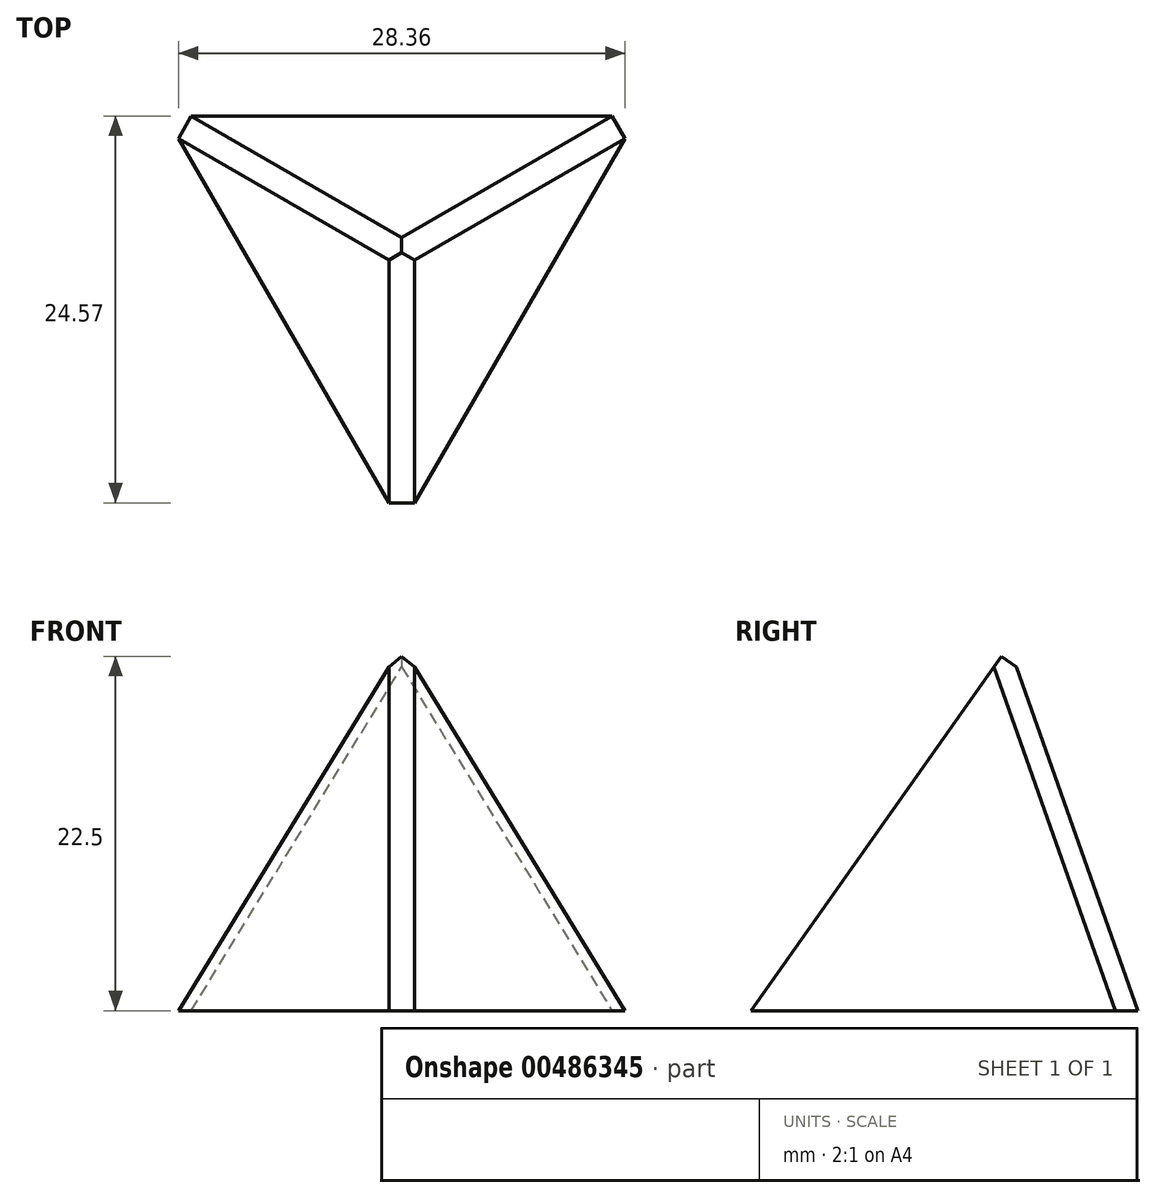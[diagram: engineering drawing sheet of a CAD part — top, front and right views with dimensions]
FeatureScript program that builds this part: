
annotation { "Feature Type Name" : "Feature", "Feature Type Description" : "" }
export const myFeature = defineFeature(function(context is Context, id is Id, definition is map)
    precondition{}
    {
        {
            var Q0;
            Q0=qCreatedBy(makeId("Top.planeOp"),FACE);
            var sketch = newSketch(context, id + "F0", { "sketchPlane" : qUnion([Q0])});
            skCircle(sketch, "E0.cCircle", {"center": v(0, 0) * mm, "radius": 8.66 * mm, "construction": true});
            skLineSegment(sketch, "E0.0", {"start": v(-15, 8.66) * mm, "end": v(15, 8.66) * mm});
            skLineSegment(sketch, "E0.1", {"start": v(15, 8.66) * mm, "end": v(0, -17.32) * mm});
            skLineSegment(sketch, "E0.2", {"start": v(0, -17.32) * mm, "end": v(-15, 8.66) * mm});
            skPoint(sketch, "E0.0.midPoint", {"position": v(0, 8.66) * mm});
            skSolve(sketch);
        }
        {
            var Q0;
            Q0 = qSketchRegion(id + "F0", true);
            extrude(context, id + "F1", {"entities" : qUnion([Q0]), "depth" : 24.5 * mm, "hasDraft" : true, "draftAngle" : 19.47 * degree, "draftPullDirection" : true});
        }
        {
            var Q0;
            Q0=makeQuery(id+"F1.opExtrude","SWEPT_EDGE",EDGE,{"disambiguationData":[OSD([sQuery(id+"F0.wireOp",EDGE,"E0.1"),sQuery(id+"F0.wireOp",EDGE,"E0.2")])]});
            var Q1;
            Q1=makeQuery(id+"F1.opExtrude","SWEPT_EDGE",EDGE,{"disambiguationData":[OSD([sQuery(id+"F0.wireOp",EDGE,"E0.0"),sQuery(id+"F0.wireOp",EDGE,"E0.1")])]});
            var Q2;
            Q2=makeQuery(id+"F1.opExtrude","SWEPT_EDGE",EDGE,{"disambiguationData":[OSD([sQuery(id+"F0.wireOp",EDGE,"E0.0"),sQuery(id+"F0.wireOp",EDGE,"E0.2")])]});
            chamfer(context, id + "F2", {"entities" : qUnion([Q0, Q1, Q2]), "width" : 1 * mm, "tangentPropagation" : true});
        }
    });
